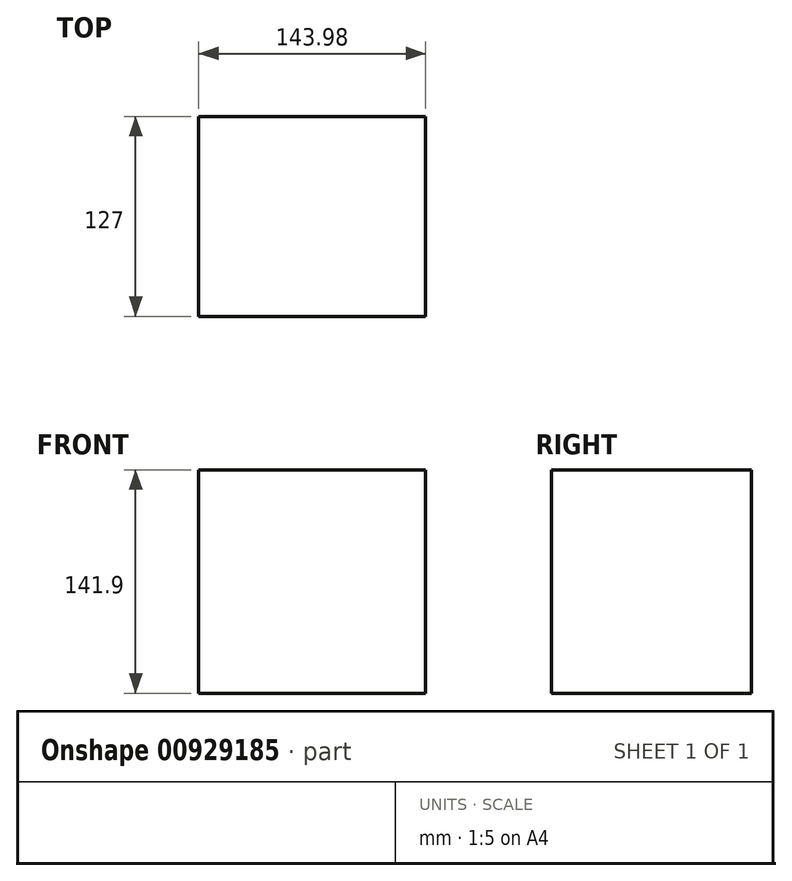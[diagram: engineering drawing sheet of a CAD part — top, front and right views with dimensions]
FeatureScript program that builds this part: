
annotation { "Feature Type Name" : "Feature", "Feature Type Description" : "" }
export const myFeature = defineFeature(function(context is Context, id is Id, definition is map)
    precondition{}
    {
        {
            var Q0;
            Q0=qCreatedBy(makeId("Front.planeOp"),FACE);
            var sketch = newSketch(context, id + "F0", { "sketchPlane" : qUnion([Q0])});
            skLineSegment(sketch, "E0.bottom", {"start": v(71.99, 70.95) * mm, "end": v(-71.99, 70.95) * mm});
            skLineSegment(sketch, "E0.top", {"start": v(71.99, -70.95) * mm, "end": v(-71.99, -70.95) * mm});
            skLineSegment(sketch, "E0.left", {"start": v(71.99, 70.95) * mm, "end": v(71.99, -70.95) * mm});
            skLineSegment(sketch, "E0.right", {"start": v(-71.99, 70.95) * mm, "end": v(-71.99, -70.95) * mm});
            skPoint(sketch, "E0.middle", {"position": v(0, 0) * mm});
            skSolve(sketch);
        }
        {
            var Q0;
            Q0=makeQuery(id+"F0.imprint","IMPRINT",FACE,{"disambiguationData":[TD([[makeQuery(id+"F0.imprint","IMPRINT",EDGE,{"derivedFrom":sQuery(id+"F0.wireOp",EDGE,"E0.bottom")}),1.0]])]});
            extrude(context, id + "F1", {"entities" : qUnion([Q0]), "endBound" : BoundingType.SYMMETRIC, "depth" : 127 * mm, "offsetDistance" : 25.4 * mm});
        }
    });
